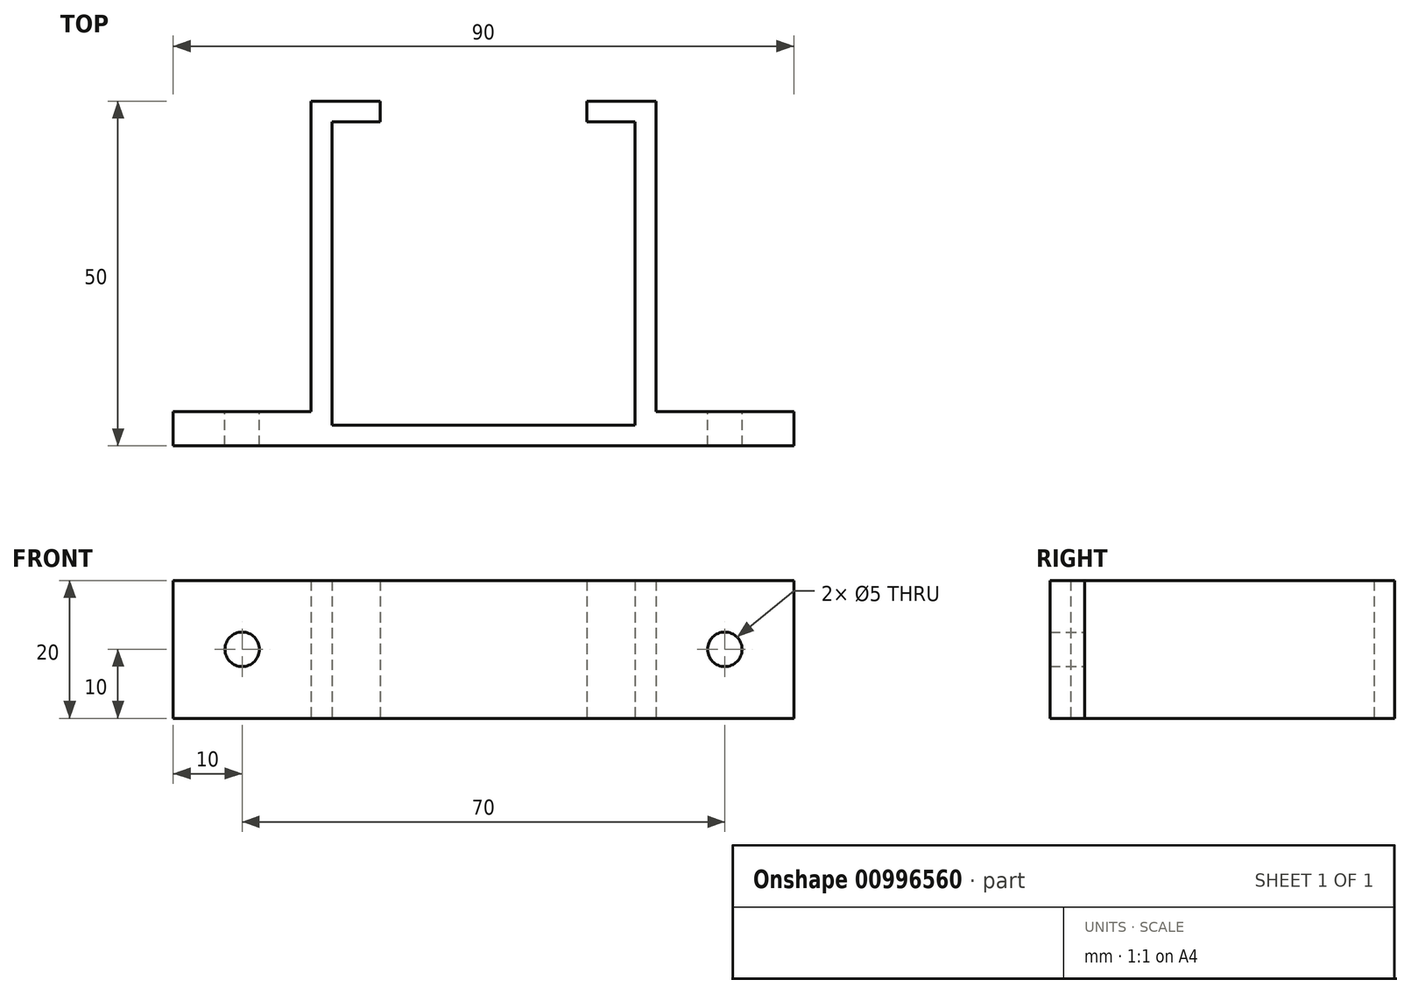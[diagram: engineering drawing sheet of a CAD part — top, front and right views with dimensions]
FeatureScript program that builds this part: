
annotation { "Feature Type Name" : "Feature", "Feature Type Description" : "" }
export const myFeature = defineFeature(function(context is Context, id is Id, definition is map)
    precondition{}
    {
        {
            var Q0;
            Q0=qCreatedBy(makeId("Top.planeOp"),FACE);
            var sketch = newSketch(context, id + "F0", { "sketchPlane" : qUnion([Q0])});
            skLineSegment(sketch, "E0.bottom", {"start": v(0, 0) * mm, "end": v(44, 0) * mm});
            skLineSegment(sketch, "E0.top", {"start": v(0, 44) * mm, "end": v(44, 44) * mm});
            skLineSegment(sketch, "E0.left", {"start": v(0, 0) * mm, "end": v(0, 44) * mm});
            skLineSegment(sketch, "E0.right", {"start": v(44, 0) * mm, "end": v(44, 44) * mm});
            skLineSegment(sketch, "E1.bottom", {"start": v(-3, 47) * mm, "end": v(47, 47) * mm});
            skLineSegment(sketch, "E1.top", {"start": v(-3, -3) * mm, "end": v(47, -3) * mm});
            skLineSegment(sketch, "E1.left", {"start": v(-3, 47) * mm, "end": v(-3, -3) * mm});
            skLineSegment(sketch, "E1.right", {"start": v(47, 47) * mm, "end": v(47, -3) * mm});
            skLineSegment(sketch, "E2.bottom", {"start": v(47, -3) * mm, "end": v(67, -3) * mm});
            skLineSegment(sketch, "E2.top", {"start": v(47, 2) * mm, "end": v(67, 2) * mm});
            skLineSegment(sketch, "E2.left", {"start": v(47, -3) * mm, "end": v(47, 2) * mm});
            skLineSegment(sketch, "E2.right", {"start": v(67, -3) * mm, "end": v(67, 2) * mm});
            skLineSegment(sketch, "E3.bottom", {"start": v(-3, -3) * mm, "end": v(-23, -3) * mm});
            skLineSegment(sketch, "E3.top", {"start": v(-3, 2) * mm, "end": v(-23, 2) * mm});
            skLineSegment(sketch, "E3.left", {"start": v(-3, -3) * mm, "end": v(-3, 2) * mm});
            skLineSegment(sketch, "E3.right", {"start": v(-23, -3) * mm, "end": v(-23, 2) * mm});
            skLineSegment(sketch, "E4.bottom", {"start": v(7, 47) * mm, "end": v(37, 47) * mm});
            skLineSegment(sketch, "E4.top", {"start": v(7, 44) * mm, "end": v(37, 44) * mm});
            skLineSegment(sketch, "E4.left", {"start": v(7, 47) * mm, "end": v(7, 44) * mm});
            skLineSegment(sketch, "E4.right", {"start": v(37, 47) * mm, "end": v(37, 44) * mm});
            skSolve(sketch);
        }
        {
            var Q0;
            Q0=makeQuery(id+"F0.imprint","IMPRINT",FACE,{"disambiguationData":[TD([[makeQuery(id+"F0.imprint","IMPRINT",EDGE,{"derivedFrom":sQuery(id+"F0.wireOp",EDGE,"E0.bottom")}),-1.0]])]});
            var Q1;
            Q1=makeQuery(id+"F0.imprint","IMPRINT",FACE,{"disambiguationData":[TD([[makeQuery(id+"F0.imprint","IMPRINT",EDGE,{"derivedFrom":sQuery(id+"F0.wireOp",EDGE,"E3.bottom")}),-1.0]])]});
            var Q2;
            Q2=makeQuery(id+"F0.imprint","IMPRINT",FACE,{"disambiguationData":[TD([[makeQuery(id+"F0.imprint","IMPRINT",EDGE,{"derivedFrom":sQuery(id+"F0.wireOp",EDGE,"E2.bottom")}),1.0]])]});
            extrude(context, id + "F1", {"entities" : qUnion([Q0, Q1, Q2]), "depth" : 20 * mm, "offsetDistance" : 25 * mm});
        }
        {
            var Q0;
            Q0=makeQuery(id+"F1.opExtrude","SWEPT_FACE",FACE,{"disambiguationData":[OSD([sQuery(id+"F0.wireOp",EDGE,"E2.top")])]});
            var sketch = newSketch(context, id + "F2", { "sketchPlane" : qUnion([Q0])});
            skCircle(sketch, "E5", {"center": v(-57, 10) * mm, "radius": 2.5 * mm});
            skCircle(sketch, "E6", {"center": v(13, 10) * mm, "radius": 2.5 * mm});
            skSolve(sketch);
        }
        {
            var Q0;
            Q0=makeQuery(id+"F2.imprint","IMPRINT",FACE,{"disambiguationData":[TD([[makeQuery(id+"F2.imprint","IMPRINT",EDGE,{"derivedFrom":sQuery(id+"F2.wireOp",EDGE,"E5")}),1.0]])]});
            var Q1;
            Q1=makeQuery(id+"F2.imprint","IMPRINT",FACE,{"disambiguationData":[TD([[makeQuery(id+"F2.imprint","IMPRINT",EDGE,{"derivedFrom":sQuery(id+"F2.wireOp",EDGE,"E6")}),1.0]])]});
            extrude(context, id + "F3", {"entities" : qUnion([Q0, Q1]), "operationType" : NewBodyOperationType.REMOVE, "oppositeDirection" : true, "depth" : 25 * mm, "offsetDistance" : 25 * mm});
        }
    });
